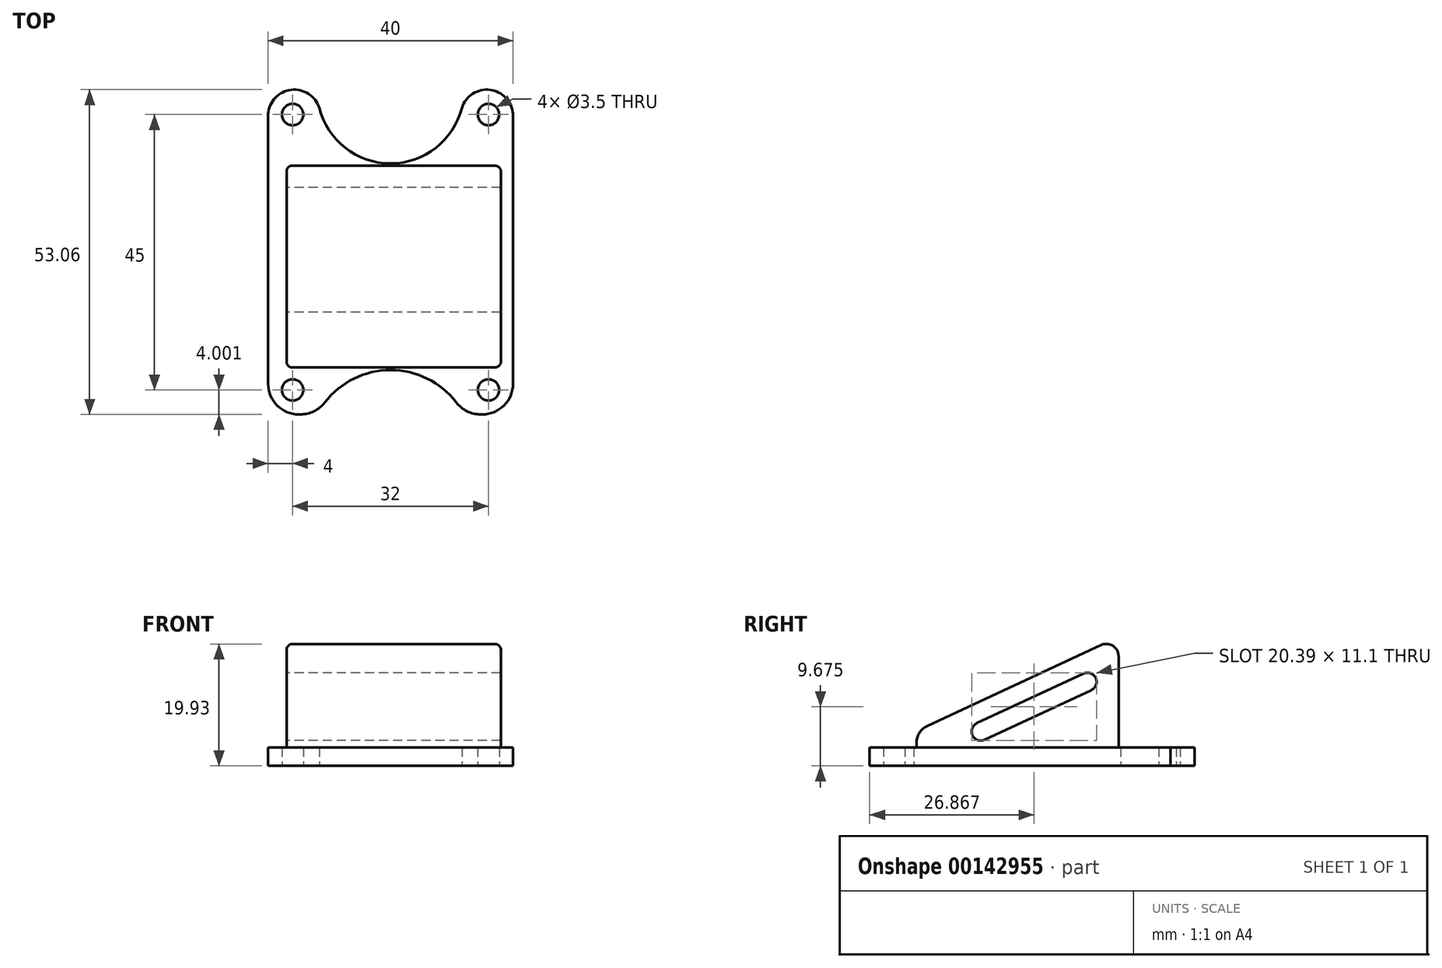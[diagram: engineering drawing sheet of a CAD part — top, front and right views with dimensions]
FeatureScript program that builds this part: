
annotation { "Feature Type Name" : "Feature", "Feature Type Description" : "" }
export const myFeature = defineFeature(function(context is Context, id is Id, definition is map)
    precondition{}
    {
        {
            var Q0;
            Q0=qCreatedBy(makeId("Top.planeOp"),FACE);
            var sketch = newSketch(context, id + "F0", { "sketchPlane" : qUnion([Q0])});
            skLineSegment(sketch, "E0.top", {"start": v(-15.52, -27.89) * mm, "end": v(-15.23, -27.89) * mm});
            skLineSegment(sketch, "E0.left", {"start": v(-20.52, 21.23) * mm, "end": v(-20.52, -22.89) * mm});
            skLineSegment(sketch, "E0.right", {"start": v(19.48, 21.23) * mm, "end": v(19.48, -22.89) * mm});
            skCircle(sketch, "E1", {"center": v(-16.52, 21.11) * mm, "radius": 1.75 * mm});
            skCircle(sketch, "E2", {"center": v(-16.52, -23.89) * mm, "radius": 1.75 * mm});
            skCircle(sketch, "E3", {"center": v(15.48, -23.89) * mm, "radius": 1.75 * mm});
            skCircle(sketch, "E4", {"center": v(15.48, 21.11) * mm, "radius": 1.75 * mm});
            skArc(sketch, "E5", {"start": v(-12.17, 22.23) * mm, "mid": v(-0.52, 13.11) * mm, "end": v(11.13, 22.23) * mm});
            skArc(sketch, "E6", {"start": v(10.23, -25.94) * mm, "mid": v(-0.52, -20.64) * mm, "end": v(-11.27, -25.94) * mm});
            skLineSegment(sketch, "E7.trimOffspring", {"start": v(14.2, -27.89) * mm, "end": v(14.48, -27.89) * mm});
            skPoint(sketch, "E8.visualSharp", {"position": v(-12.52, -27.89) * mm});
            skArc(sketch, "E8.filletArc", {"start": v(-15.23, -27.89) * mm, "mid": v(-13.02, -27.37) * mm, "end": v(-11.27, -25.94) * mm});
            skPoint(sketch, "E9.visualSharp", {"position": v(11.48, -27.89) * mm});
            skArc(sketch, "E9.filletArc", {"start": v(10.23, -25.94) * mm, "mid": v(11.98, -27.37) * mm, "end": v(14.2, -27.89) * mm});
            skPoint(sketch, "E10.visualSharp", {"position": v(19.48, -27.89) * mm});
            skArc(sketch, "E10.filletArc", {"start": v(14.48, -27.89) * mm, "mid": v(18.02, -26.42) * mm, "end": v(19.48, -22.89) * mm});
            skPoint(sketch, "E11.visualSharp", {"position": v(-20.52, -27.89) * mm});
            skArc(sketch, "E11.filletArc", {"start": v(-20.52, -22.89) * mm, "mid": v(-19.06, -26.42) * mm, "end": v(-15.52, -27.89) * mm});
            skArc(sketch, "E12", {"start": v(-12.17, 22.23) * mm, "mid": v(-16.75, 25.14) * mm, "end": v(-20.52, 21.23) * mm});
            skArc(sketch, "E13.MirrorCS", {"start": v(11.13, 22.23) * mm, "mid": v(15.71, 25.14) * mm, "end": v(19.48, 21.23) * mm});
            skPoint(sketch, "E14.orphan", {"position": v(19.48, 25.11) * mm});
            skPoint(sketch, "E15.orphan", {"position": v(-20.52, 25.11) * mm});
            skSolve(sketch);
        }
        {
            var Q0;
            Q0=makeQuery(id+"F0.imprint","IMPRINT",FACE,{"disambiguationData":[TD([[makeQuery(id+"F0.imprint","IMPRINT",EDGE,{"derivedFrom":sQuery(id+"F0.wireOp",EDGE,"E0.top")}),1.0]])]});
            extrude(context, id + "F1", {"entities" : qUnion([Q0]), "depth" : 3 * mm});
        }
        {
            var Q0;
            Q0=qCreatedBy(makeId("Right.planeOp"),FACE);
            var sketch = newSketch(context, id + "F2", { "sketchPlane" : qUnion([Q0])});
            skLineSegment(sketch, "E16", {"start": v(-20.23, 2.69) * mm, "end": v(12.77, 2.69) * mm});
            skLineSegment(sketch, "E17", {"start": v(12.77, 2.69) * mm, "end": v(12.77, 17.93) * mm});
            skLineSegment(sketch, "E18", {"start": v(9.93, 19.74) * mm, "end": v(-18.5, 6.5) * mm});
            skLineSegment(sketch, "E19", {"start": v(-20.23, 3.78) * mm, "end": v(-20.23, 2.69) * mm});
            skLineSegment(sketch, "E20.0", {"start": v(7.04, 15.09) * mm, "end": v(-10.35, 6.98) * mm});
            skLineSegment(sketch, "E21.trimOffspring", {"start": v(8.3, 12.37) * mm, "end": v(-9.09, 4.26) * mm});
            skArc(sketch, "E22", {"start": v(-10.35, 6.98) * mm, "mid": v(-11.08, 4.99) * mm, "end": v(-9.09, 4.26) * mm});
            skArc(sketch, "E23", {"start": v(8.3, 12.37) * mm, "mid": v(9.03, 14.36) * mm, "end": v(7.04, 15.09) * mm});
            skPoint(sketch, "E24.visualSharp", {"position": v(-20.23, 5.69) * mm});
            skArc(sketch, "E24.filletArc", {"start": v(-18.5, 6.5) * mm, "mid": v(-19.76, 5.39) * mm, "end": v(-20.23, 3.78) * mm});
            skPoint(sketch, "E25.visualSharp", {"position": v(12.77, 21.07) * mm});
            skArc(sketch, "E25.filletArc", {"start": v(12.77, 17.93) * mm, "mid": v(11.85, 19.62) * mm, "end": v(9.93, 19.74) * mm});
            skSolve(sketch);
        }
        {
            var Q0;
            Q0=makeQuery(id+"F2.imprint","IMPRINT",FACE,{"disambiguationData":[TD([[makeQuery(id+"F2.imprint","IMPRINT",EDGE,{"derivedFrom":sQuery(id+"F2.wireOp",EDGE,"E16")}),1.0]])]});
            extrude(context, id + "F3", {"entities" : qUnion([Q0]), "operationType" : NewBodyOperationType.ADD, "depth" : 35 * mm, "symmetric" : true});
        }
        {
            var Q0;
            Q0=makeQuery(id+"F3.opExtrude","CAP_EDGE",EDGE,{"disambiguationData":[OSD([sQuery(id+"F2.wireOp",EDGE,"E18")])],"isStart":false});
            var Q1;
            Q1=makeQuery(id+"F3.opExtrude","CAP_EDGE",EDGE,{"disambiguationData":[OSD([sQuery(id+"F2.wireOp",EDGE,"E18")])],"isStart":true});
            fillet(context, id + "F4", {"entities" : qUnion([Q0, Q1]), "radius" : 1 * mm, "tangentPropagation" : true, "allowEdgeOverflow" : false});
        }
    });
